# Revit family: Universalkonsole mit Knoten 350x550x 4
name_source: partatom
category: HLS-Bauteile
revit_build: Autodesk Revit 2017 (Build: 20190507_1515(x64)
units: mm (PartAtom-declared; Revit-internal decimal feet)

## family parameters
Basisbauteil = Fläche
Beim Laden mit Abzugskörper schneiden = Nein
Bemaßung runder Anschluss = Durchmesser verwenden
Gemeinsam genutzt = Ja
Raumberechnungspunkt = Nein
Teiletyp = Normal

## types (1)
- Universalkonsole mit Knoten 350x550x 4
    Abmessung = 350 x 550 x 4 mm
    Artikelnummer = 081424301
    Ausführung = mit Streben
    EAN = 4250928419934
    Fabrikat = MEFA
    Firma = MEFA Befestigungs- und Montagesysteme GmbH
    Gewicht = 4.14 kg
    Gewicht pro Bauteil = 4.14 kg
    Höhe = 350 mm
    Kurztext1 = Universalkonsole mit 2 Streben
    Kurztext2 = 350 x 550 x 4 mm
    L1 = 350 mm  [stored 1.14829 ft]
    L2 = 550 mm
    Länge = 550 mm
    Material = Stahl
    Materialname = S235
    Mengeneinheit = St
    Oberflaeche = galvanisch verzinkt
    Stärke = 4 mm  [stored 0.0131234 ft]
    Vorgabe-Ansicht = 1219 mm
    max. zul. Last F1 = 1.46 kip
    max. zul. Last F2 = 0.83 kip
    vpe = 5 St

note: [stored X ft] marks values corroborated as IEEE doubles in the binary element streams (Revit-internal decimal feet)
